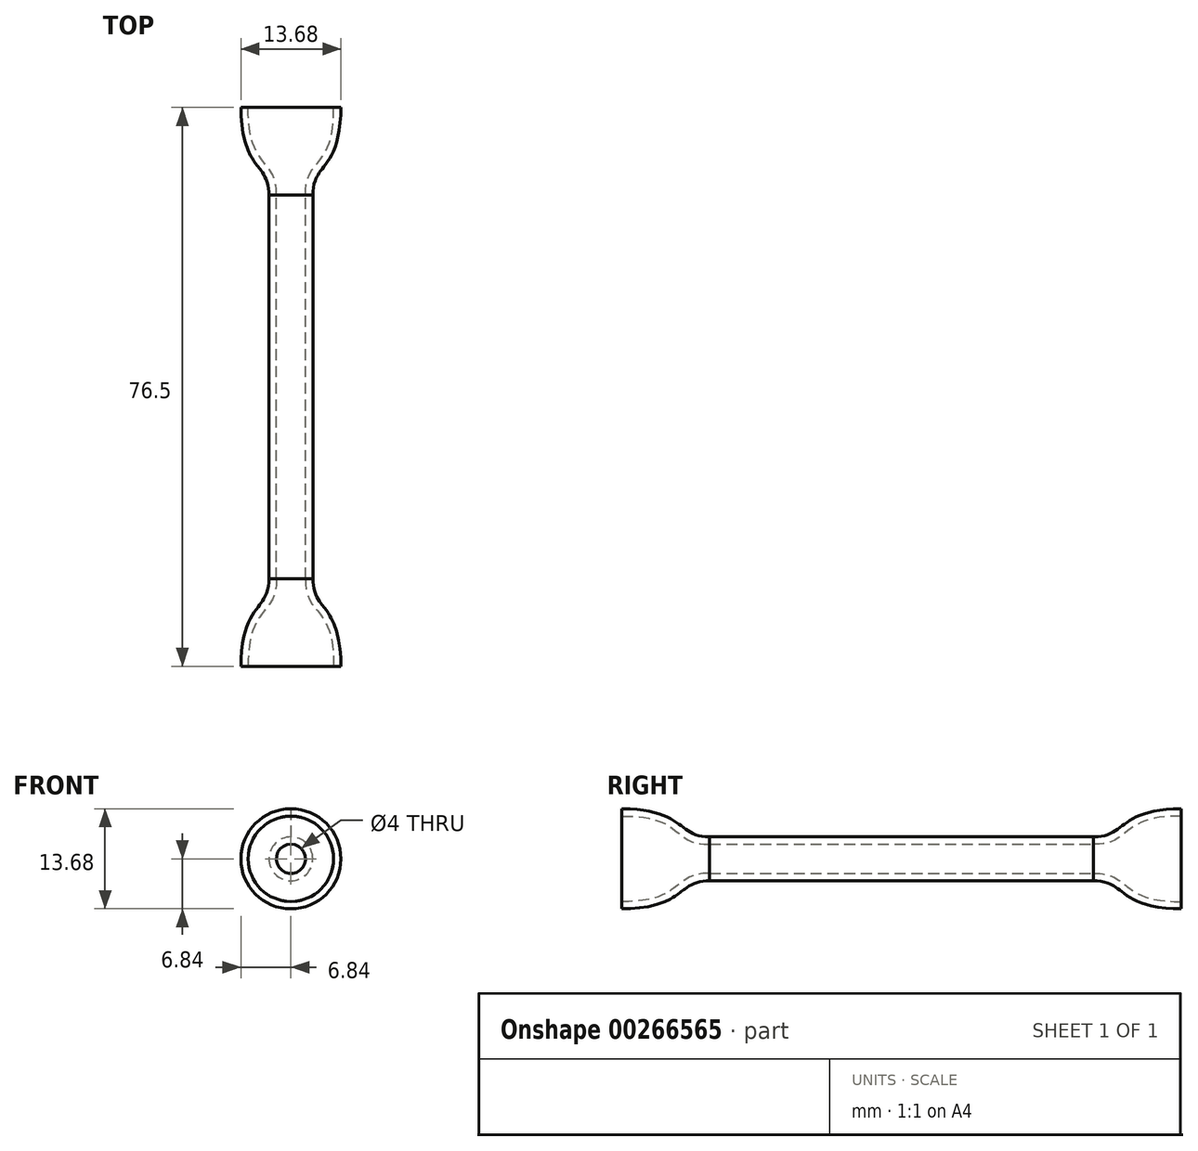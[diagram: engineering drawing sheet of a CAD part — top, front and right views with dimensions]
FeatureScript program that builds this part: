
annotation { "Feature Type Name" : "Feature", "Feature Type Description" : "" }
export const myFeature = defineFeature(function(context is Context, id is Id, definition is map)
    precondition{}
    {
        {
            var Q0;
            Q0=qCreatedBy(makeId("Right.planeOp"),FACE);
            var sketch = newSketch(context, id + "F0", { "sketchPlane" : qUnion([Q0])});
            skLineSegment(sketch, "E0", {"start": v(0, 0) * mm, "end": v(0, 6.84) * mm});
            skLineSegment(sketch, "E1", {"start": v(38.25, 0) * mm, "end": v(38.25, 3) * mm});
            skLineSegment(sketch, "E2", {"start": v(12, 0) * mm, "end": v(12, 3) * mm, "construction": true});
            skFitSpline(sketch, "E3", {"points": [v(0, 6.84) * mm, v(12, 3) * mm], "startDerivative": vector(26.3, -0.21) * mm, "endDerivative": vector(13.62, 0) * mm});
            skLineSegment(sketch, "E4", {"start": v(12, 3) * mm, "end": v(38.25, 3) * mm});
            skLineSegment(sketch, "E5", {"start": v(38.25, 0) * mm, "end": v(0, 0) * mm});
            skLineSegment(sketch, "E6.0", {"start": v(12, 2) * mm, "end": v(38.25, 2) * mm});
            skFitSpline(sketch, "E6.1", {"points": [v(0, 5.84) * mm, v(1.05, 5.83) * mm, v(2.84, 5.7) * mm, v(4.74, 5.28) * mm, v(6.04, 4.72) * mm, v(7.02, 4.09) * mm, v(7.9, 3.4) * mm, v(8.91, 2.68) * mm, v(10.24, 2.13) * mm, v(11.36, 2) * mm, v(12, 2) * mm]});
            skLineSegment(sketch, "E7", {"start": v(12, 2) * mm, "end": v(12, 0) * mm});
            skSolve(sketch);
        }
        {
            var Q0;
            {var subQ0=sQuery(id+"F0.wireOp",EDGE,"E3");Q0=makeQuery(id+"F0.imprint","IMPRINT",FACE,{"disambiguationData":[TD([[makeQuery(id+"F0.imprint","IMPRINT",EDGE,{"derivedFrom":subQ0}),-1.0]])]});}
            var Q1;
            Q1=sQuery(id+"F0.wireOp",EDGE,"E5");
            revolve(context, id + "F1", {"entities" : qUnion([Q0]), "axis" : qUnion([Q1]), "revolveType" : RevolveType.FULL});
        }
        {
            var Q0;
            Q0=makeQuery(id+"F1.opRevolve","SWEPT_FACE",FACE,{"disambiguationData":[OSD([sQuery(id+"F0.wireOp",EDGE,"E0")])]});
            var sketch = newSketch(context, id + "F2", { "sketchPlane" : qUnion([Q0])});
            skCircle(sketch, "E8", {"center": v(0, 0) * mm, "radius": 0.9 * mm});
            skSolve(sketch);
        }
        {
            var Q0;
            Q0 = qSketchRegion(id + "F2", true);
            extrude(context, id + "F3", {"entities" : qUnion([Q0]), "operationType" : NewBodyOperationType.REMOVE, "oppositeDirection" : true, "depth" : 8 * mm});
        }
        {
            var Q0;
            Q0=makeQuery(id+"F1.opRevolve","SWEPT_BODY",BODY,{"disambiguationData":[OSD([sQuery(id+"F0.wireOp",EDGE,"E0"),sQuery(id+"F0.wireOp",EDGE,"E1"),sQuery(id+"F0.wireOp",EDGE,"E3"),sQuery(id+"F0.wireOp",EDGE,"E4"),sQuery(id+"F0.wireOp",EDGE,"E5"),sQuery(id+"F0.wireOp",EDGE,"E6.0"),sQuery(id+"F0.wireOp",EDGE,"E7")])]});
            var Q1;
            Q1=makeQuery(id+"F1.opRevolve","SWEPT_FACE",FACE,{"disambiguationData":[OSD([sQuery(id+"F0.wireOp",EDGE,"E1")])]});
            mirror(context, id + "F4", {"operationType" : NewBodyOperationType.ADD, "entities" : qUnion([Q0]), "mirrorPlane" : qUnion([Q1])});
        }
    });
